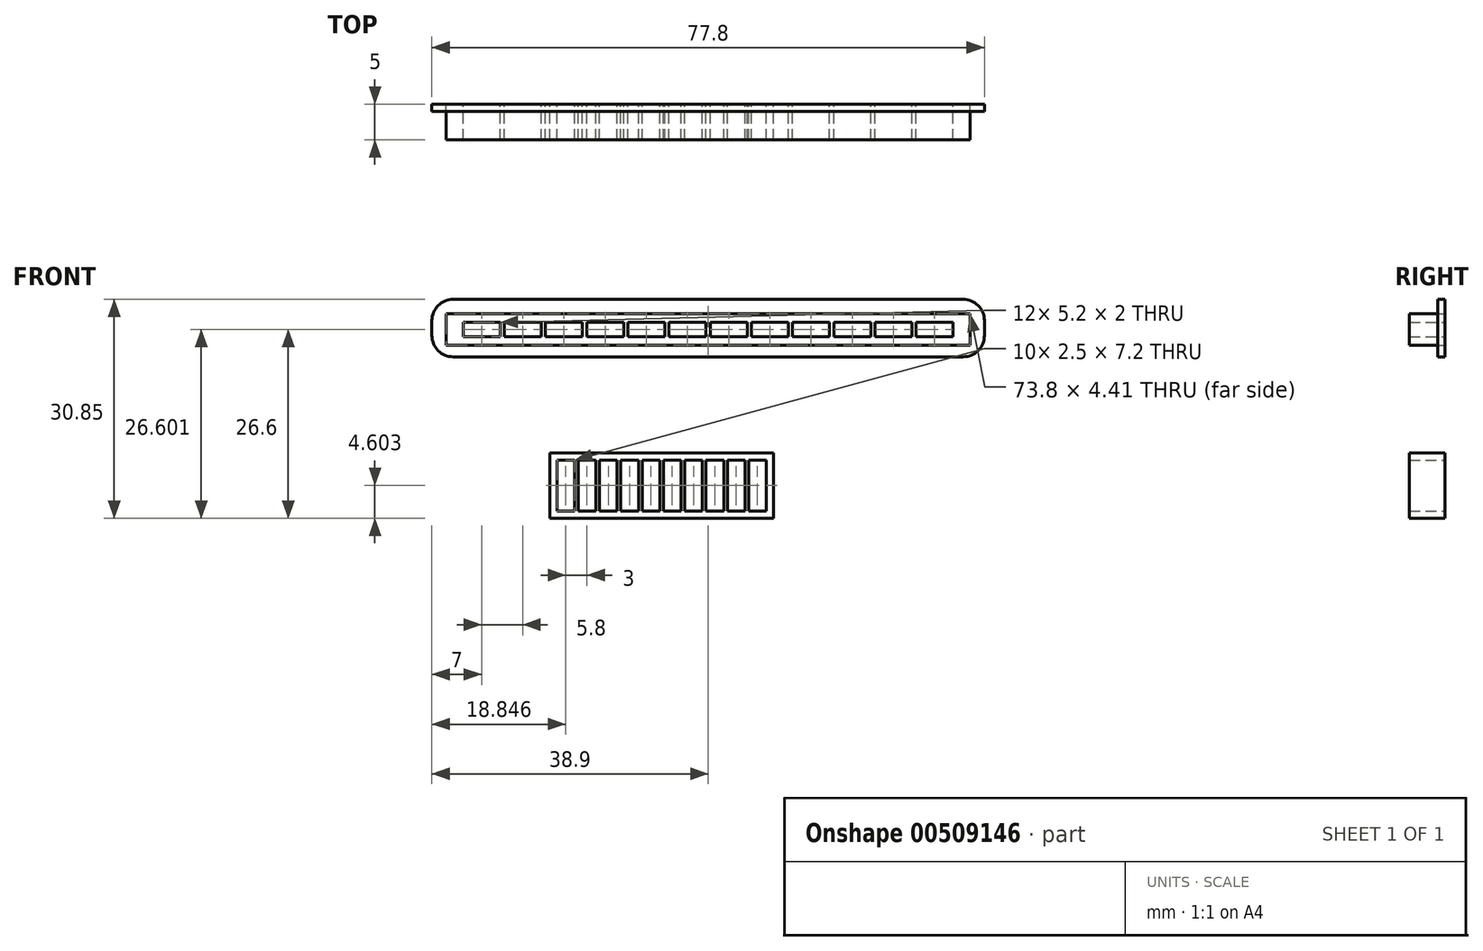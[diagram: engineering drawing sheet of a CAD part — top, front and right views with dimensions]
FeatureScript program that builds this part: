
annotation { "Feature Type Name" : "Feature", "Feature Type Description" : "" }
export const myFeature = defineFeature(function(context is Context, id is Id, definition is map)
    precondition{}
    {
        {
            var Q0;
            Q0=qCreatedBy(makeId("Front.planeOp"),FACE);
            var sketch = newSketch(context, id + "F0", { "sketchPlane" : qUnion([Q0])});
            skPoint(sketch, "E0.middle", {"position": v(0, 0) * mm});
            skLineSegment(sketch, "E1.bottom", {"start": v(-34.5, 0.8) * mm, "end": v(-29.3, 0.8) * mm});
            skLineSegment(sketch, "E1.top", {"start": v(-34.5, -1.2) * mm, "end": v(-29.3, -1.2) * mm});
            skLineSegment(sketch, "E1.left", {"start": v(-34.5, 0.8) * mm, "end": v(-34.5, -1.2) * mm});
            skLineSegment(sketch, "E1.right", {"start": v(-29.3, 0.8) * mm, "end": v(-29.3, -1.2) * mm});
            skLineSegment(sketch, "E2.bottom", {"start": v(-28.7, 0.8) * mm, "end": v(-23.5, 0.8) * mm});
            skLineSegment(sketch, "E2.top", {"start": v(-28.7, -1.2) * mm, "end": v(-23.5, -1.2) * mm});
            skLineSegment(sketch, "E2.left", {"start": v(-28.7, 0.8) * mm, "end": v(-28.7, -1.2) * mm});
            skLineSegment(sketch, "E2.right", {"start": v(-23.5, 0.8) * mm, "end": v(-23.5, -1.2) * mm});
            skLineSegment(sketch, "E3.bottom", {"start": v(-22.9, 0.8) * mm, "end": v(-17.7, 0.8) * mm});
            skLineSegment(sketch, "E3.top", {"start": v(-22.9, -1.2) * mm, "end": v(-17.7, -1.2) * mm});
            skLineSegment(sketch, "E3.left", {"start": v(-22.9, 0.8) * mm, "end": v(-22.9, -1.2) * mm});
            skLineSegment(sketch, "E3.right", {"start": v(-17.7, 0.8) * mm, "end": v(-17.7, -1.2) * mm});
            skLineSegment(sketch, "E4.bottom", {"start": v(-17.1, 0.8) * mm, "end": v(-11.9, 0.8) * mm});
            skLineSegment(sketch, "E4.top", {"start": v(-17.1, -1.2) * mm, "end": v(-11.9, -1.2) * mm});
            skLineSegment(sketch, "E4.left", {"start": v(-17.1, 0.8) * mm, "end": v(-17.1, -1.2) * mm});
            skLineSegment(sketch, "E4.right", {"start": v(-11.9, 0.8) * mm, "end": v(-11.9, -1.2) * mm});
            skLineSegment(sketch, "E5.bottom", {"start": v(-11.3, 0.8) * mm, "end": v(-6.1, 0.8) * mm});
            skLineSegment(sketch, "E5.top", {"start": v(-11.3, -1.2) * mm, "end": v(-6.1, -1.2) * mm});
            skLineSegment(sketch, "E5.left", {"start": v(-11.3, 0.8) * mm, "end": v(-11.3, -1.2) * mm});
            skLineSegment(sketch, "E5.right", {"start": v(-6.1, 0.8) * mm, "end": v(-6.1, -1.2) * mm});
            skLineSegment(sketch, "E6.bottom", {"start": v(-5.5, 0.8) * mm, "end": v(-0.3, 0.8) * mm});
            skLineSegment(sketch, "E6.top", {"start": v(-5.5, -1.2) * mm, "end": v(-0.3, -1.2) * mm});
            skLineSegment(sketch, "E6.left", {"start": v(-5.5, 0.8) * mm, "end": v(-5.5, -1.2) * mm});
            skLineSegment(sketch, "E6.right", {"start": v(-0.3, 0.8) * mm, "end": v(-0.3, -1.2) * mm});
            skLineSegment(sketch, "E7.bottom", {"start": v(0.3, 0.8) * mm, "end": v(5.5, 0.8) * mm});
            skLineSegment(sketch, "E7.top", {"start": v(0.3, -1.2) * mm, "end": v(5.5, -1.2) * mm});
            skLineSegment(sketch, "E7.left", {"start": v(0.3, 0.8) * mm, "end": v(0.3, -1.2) * mm});
            skLineSegment(sketch, "E7.right", {"start": v(5.5, 0.8) * mm, "end": v(5.5, -1.2) * mm});
            skLineSegment(sketch, "E8.bottom", {"start": v(6.1, 0.8) * mm, "end": v(11.3, 0.8) * mm});
            skLineSegment(sketch, "E8.top", {"start": v(6.1, -1.2) * mm, "end": v(11.3, -1.2) * mm});
            skLineSegment(sketch, "E8.left", {"start": v(6.1, 0.8) * mm, "end": v(6.1, -1.2) * mm});
            skLineSegment(sketch, "E8.right", {"start": v(11.3, 0.8) * mm, "end": v(11.3, -1.2) * mm});
            skLineSegment(sketch, "E9.bottom", {"start": v(11.9, 0.8) * mm, "end": v(17.1, 0.8) * mm});
            skLineSegment(sketch, "E9.top", {"start": v(11.9, -1.2) * mm, "end": v(17.1, -1.2) * mm});
            skLineSegment(sketch, "E9.left", {"start": v(11.9, 0.8) * mm, "end": v(11.9, -1.2) * mm});
            skLineSegment(sketch, "E9.right", {"start": v(17.1, 0.8) * mm, "end": v(17.1, -1.2) * mm});
            skLineSegment(sketch, "E10.bottom", {"start": v(17.7, 0.8) * mm, "end": v(22.9, 0.8) * mm});
            skLineSegment(sketch, "E10.top", {"start": v(17.7, -1.2) * mm, "end": v(22.9, -1.2) * mm});
            skLineSegment(sketch, "E10.left", {"start": v(17.7, 0.8) * mm, "end": v(17.7, -1.2) * mm});
            skLineSegment(sketch, "E10.right", {"start": v(22.9, 0.8) * mm, "end": v(22.9, -1.2) * mm});
            skLineSegment(sketch, "E11.bottom", {"start": v(23.5, 0.8) * mm, "end": v(28.7, 0.8) * mm});
            skLineSegment(sketch, "E11.top", {"start": v(23.5, -1.2) * mm, "end": v(28.7, -1.2) * mm});
            skLineSegment(sketch, "E11.left", {"start": v(23.5, 0.8) * mm, "end": v(23.5, -1.2) * mm});
            skLineSegment(sketch, "E11.right", {"start": v(28.7, 0.8) * mm, "end": v(28.7, -1.2) * mm});
            skLineSegment(sketch, "E12.bottom", {"start": v(29.3, 0.8) * mm, "end": v(34.5, 0.8) * mm});
            skLineSegment(sketch, "E12.top", {"start": v(29.3, -1.2) * mm, "end": v(34.5, -1.2) * mm});
            skLineSegment(sketch, "E12.left", {"start": v(29.3, 0.8) * mm, "end": v(29.3, -1.2) * mm});
            skLineSegment(sketch, "E12.right", {"start": v(34.5, 0.8) * mm, "end": v(34.5, -1.2) * mm});
            skLineSegment(sketch, "E13.top", {"start": v(-36.9, -2.4) * mm, "end": v(36.9, -2.4) * mm});
            skLineSegment(sketch, "E13.left", {"start": v(-36.9, 2) * mm, "end": v(-36.9, -2.4) * mm});
            skLineSegment(sketch, "E13.right", {"start": v(36.9, 2) * mm, "end": v(36.9, -2.4) * mm});
            skLineSegment(sketch, "E14", {"start": v(-36.9, 2) * mm, "end": v(36.9, 2) * mm});
            skSolve(sketch);
        }
        {
            var Q0;
            {var subQ6=sQuery(id+"F0.wireOp",EDGE,"E1.left");Q0=makeQuery(id+"F0.imprint","IMPRINT",FACE,{"disambiguationData":[TD([[makeQuery(id+"F0.imprint","IMPRINT",EDGE,{"derivedFrom":subQ6}),-1.0]])]});}
            var Q1;
            {var subQ0=sQuery(id+"F0.wireOp",EDGE,"E0.right");Q1=makeQuery(id+"F0.imprint","IMPRINT",FACE,{"disambiguationData":[TD([[makeQuery(id+"F0.imprint","IMPRINT",EDGE,{"derivedFrom":subQ0}),1.0]])]});}
            var Q2;
            {var subQ8=sQuery(id+"F0.wireOp",EDGE,"E0.right");Q2=makeQuery(id+"F0.imprint","IMPRINT",FACE,{"disambiguationData":[TD([[makeQuery(id+"F0.imprint","IMPRINT",EDGE,{"derivedFrom":subQ8}),-1.0]])]});}
            extrude(context, id + "F1", {"entities" : qUnion([Q0, Q1, Q2]), "depth" : 5 * mm, "offsetDistance" : 25 * mm});
        }
        {
            var Q0;
            Q0=qCreatedBy(makeId("Front.planeOp"),FACE);
            var sketch = newSketch(context, id + "F2", { "sketchPlane" : qUnion([Q0])});
            skLineSegment(sketch, "E15.bottom", {"start": v(-21.3, -18.6) * mm, "end": v(-18.8, -18.6) * mm});
            skLineSegment(sketch, "E15.top", {"start": v(-21.3, -25.8) * mm, "end": v(-18.8, -25.8) * mm});
            skLineSegment(sketch, "E15.left", {"start": v(-21.3, -18.6) * mm, "end": v(-21.3, -25.8) * mm});
            skLineSegment(sketch, "E15.right", {"start": v(-18.8, -18.6) * mm, "end": v(-18.8, -25.8) * mm});
            skLineSegment(sketch, "E16.bottom", {"start": v(-18.3, -18.6) * mm, "end": v(-15.8, -18.6) * mm});
            skLineSegment(sketch, "E16.top", {"start": v(-18.3, -25.8) * mm, "end": v(-15.8, -25.8) * mm});
            skLineSegment(sketch, "E16.left", {"start": v(-18.3, -18.6) * mm, "end": v(-18.3, -25.8) * mm});
            skLineSegment(sketch, "E16.right", {"start": v(-15.8, -18.6) * mm, "end": v(-15.8, -25.8) * mm});
            skLineSegment(sketch, "E17.bottom", {"start": v(-15.3, -18.6) * mm, "end": v(-12.8, -18.6) * mm});
            skLineSegment(sketch, "E17.top", {"start": v(-15.3, -25.8) * mm, "end": v(-12.8, -25.8) * mm});
            skLineSegment(sketch, "E17.left", {"start": v(-15.3, -18.6) * mm, "end": v(-15.3, -25.8) * mm});
            skLineSegment(sketch, "E17.right", {"start": v(-12.8, -18.6) * mm, "end": v(-12.8, -25.8) * mm});
            skLineSegment(sketch, "E18.bottom", {"start": v(-12.3, -18.6) * mm, "end": v(-9.8, -18.6) * mm});
            skLineSegment(sketch, "E18.top", {"start": v(-12.3, -25.8) * mm, "end": v(-9.8, -25.8) * mm});
            skLineSegment(sketch, "E18.left", {"start": v(-12.3, -18.6) * mm, "end": v(-12.3, -25.8) * mm});
            skLineSegment(sketch, "E18.right", {"start": v(-9.8, -18.6) * mm, "end": v(-9.8, -25.8) * mm});
            skLineSegment(sketch, "E19.bottom", {"start": v(-9.3, -18.6) * mm, "end": v(-6.8, -18.6) * mm});
            skLineSegment(sketch, "E19.top", {"start": v(-9.3, -25.8) * mm, "end": v(-6.8, -25.8) * mm});
            skLineSegment(sketch, "E19.left", {"start": v(-9.3, -18.6) * mm, "end": v(-9.3, -25.8) * mm});
            skLineSegment(sketch, "E19.right", {"start": v(-6.8, -18.6) * mm, "end": v(-6.8, -25.8) * mm});
            skLineSegment(sketch, "E20.bottom", {"start": v(-6.3, -18.6) * mm, "end": v(-3.8, -18.6) * mm});
            skLineSegment(sketch, "E20.top", {"start": v(-6.3, -25.8) * mm, "end": v(-3.8, -25.8) * mm});
            skLineSegment(sketch, "E20.left", {"start": v(-6.3, -18.6) * mm, "end": v(-6.3, -25.8) * mm});
            skLineSegment(sketch, "E20.right", {"start": v(-3.8, -18.6) * mm, "end": v(-3.8, -25.8) * mm});
            skLineSegment(sketch, "E21.bottom", {"start": v(-3.3, -18.6) * mm, "end": v(-0.8, -18.6) * mm});
            skLineSegment(sketch, "E21.top", {"start": v(-3.3, -25.8) * mm, "end": v(-0.8, -25.8) * mm});
            skLineSegment(sketch, "E21.left", {"start": v(-3.3, -18.6) * mm, "end": v(-3.3, -25.8) * mm});
            skLineSegment(sketch, "E21.right", {"start": v(-0.8, -18.6) * mm, "end": v(-0.8, -25.8) * mm});
            skLineSegment(sketch, "E22.bottom", {"start": v(-0.3, -18.6) * mm, "end": v(2.2, -18.6) * mm});
            skLineSegment(sketch, "E22.top", {"start": v(-0.3, -25.8) * mm, "end": v(2.2, -25.8) * mm});
            skLineSegment(sketch, "E22.left", {"start": v(-0.3, -18.6) * mm, "end": v(-0.3, -25.8) * mm});
            skLineSegment(sketch, "E22.right", {"start": v(2.2, -18.6) * mm, "end": v(2.2, -25.8) * mm});
            skLineSegment(sketch, "E23.bottom", {"start": v(2.7, -18.6) * mm, "end": v(5.2, -18.6) * mm});
            skLineSegment(sketch, "E23.top", {"start": v(2.7, -25.8) * mm, "end": v(5.2, -25.8) * mm});
            skLineSegment(sketch, "E23.left", {"start": v(2.7, -18.6) * mm, "end": v(2.7, -25.8) * mm});
            skLineSegment(sketch, "E23.right", {"start": v(5.2, -18.6) * mm, "end": v(5.2, -25.8) * mm});
            skLineSegment(sketch, "E24.bottom", {"start": v(5.7, -18.6) * mm, "end": v(8.2, -18.6) * mm});
            skLineSegment(sketch, "E24.top", {"start": v(5.7, -25.8) * mm, "end": v(8.2, -25.8) * mm});
            skLineSegment(sketch, "E24.left", {"start": v(5.7, -18.6) * mm, "end": v(5.7, -25.8) * mm});
            skLineSegment(sketch, "E24.right", {"start": v(8.2, -18.6) * mm, "end": v(8.2, -25.8) * mm});
            skLineSegment(sketch, "E25.bottom", {"start": v(-22.3, -17.6) * mm, "end": v(9.2, -17.6) * mm});
            skLineSegment(sketch, "E25.top", {"start": v(-22.3, -26.8) * mm, "end": v(9.2, -26.8) * mm});
            skLineSegment(sketch, "E25.left", {"start": v(-22.3, -17.6) * mm, "end": v(-22.3, -26.8) * mm});
            skLineSegment(sketch, "E25.right", {"start": v(9.2, -17.6) * mm, "end": v(9.2, -26.8) * mm});
            skSolve(sketch);
        }
        {
            var Q0;
            Q0=makeQuery(id+"F2.imprint","IMPRINT",FACE,{"disambiguationData":[TD([[makeQuery(id+"F2.imprint","IMPRINT",EDGE,{"derivedFrom":sQuery(id+"F2.wireOp",EDGE,"E15.bottom")}),1.0]])]});
            extrude(context, id + "F3", {"entities" : qUnion([Q0]), "depth" : 5 * mm, "offsetDistance" : 25 * mm});
        }
        {
            var Q0;
            Q0=qCreatedBy(makeId("Front.planeOp"),FACE);
            var sketch = newSketch(context, id + "F4", { "sketchPlane" : qUnion([Q0])});
            skLineSegment(sketch, "E26.bottom", {"start": v(-36.9, 2) * mm, "end": v(36.9, 2) * mm});
            skLineSegment(sketch, "E26.top", {"start": v(-36.9, -2.4) * mm, "end": v(36.9, -2.4) * mm});
            skLineSegment(sketch, "E26.left", {"start": v(-36.9, 2) * mm, "end": v(-36.9, -2.4) * mm});
            skLineSegment(sketch, "E26.right", {"start": v(36.9, 2) * mm, "end": v(36.9, -2.4) * mm});
            skLineSegment(sketch, "E27.bottom", {"start": v(-38.9, 4.05) * mm, "end": v(38.9, 4.05) * mm});
            skLineSegment(sketch, "E27.top", {"start": v(-38.9, -4.05) * mm, "end": v(38.9, -4.05) * mm});
            skLineSegment(sketch, "E27.left", {"start": v(-38.9, 4.05) * mm, "end": v(-38.9, -4.05) * mm});
            skLineSegment(sketch, "E27.right", {"start": v(38.9, 4.05) * mm, "end": v(38.9, -4.05) * mm});
            skSolve(sketch);
        }
        {
            var Q0;
            Q0=makeQuery(id+"F4.imprint","IMPRINT",FACE,{"disambiguationData":[TD([[makeQuery(id+"F4.imprint","IMPRINT",EDGE,{"derivedFrom":sQuery(id+"F4.wireOp",EDGE,"E26.bottom")}),1.0]])]});
            extrude(context, id + "F5", {"entities" : qUnion([Q0]), "depth" : 1 * mm, "offsetDistance" : 25 * mm});
        }
        {
            var Q0;
            Q0=makeQuery(id+"F5.opExtrude","SWEPT_EDGE",EDGE,{"disambiguationData":[OSD([sQuery(id+"F4.wireOp",EDGE,"E27.top"),sQuery(id+"F4.wireOp",EDGE,"E27.left")])]});
            var Q1;
            Q1=makeQuery(id+"F5.opExtrude","SWEPT_EDGE",EDGE,{"disambiguationData":[OSD([sQuery(id+"F4.wireOp",EDGE,"E27.bottom"),sQuery(id+"F4.wireOp",EDGE,"E27.left")])]});
            var Q2;
            Q2=makeQuery(id+"F5.opExtrude","SWEPT_EDGE",EDGE,{"disambiguationData":[OSD([sQuery(id+"F4.wireOp",EDGE,"E27.top"),sQuery(id+"F4.wireOp",EDGE,"E27.right")])]});
            var Q3;
            Q3=makeQuery(id+"F5.opExtrude","SWEPT_EDGE",EDGE,{"disambiguationData":[OSD([sQuery(id+"F4.wireOp",EDGE,"E27.bottom"),sQuery(id+"F4.wireOp",EDGE,"E27.right")])]});
            fillet(context, id + "F6", {"entities" : qUnion([Q0, Q1, Q2, Q3]), "radius" : 3 * mm, "tangentPropagation" : true, "allowEdgeOverflow" : false});
        }
    });
